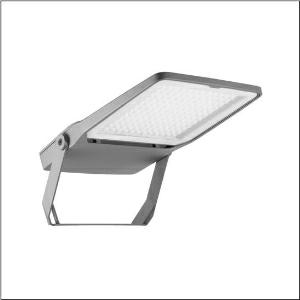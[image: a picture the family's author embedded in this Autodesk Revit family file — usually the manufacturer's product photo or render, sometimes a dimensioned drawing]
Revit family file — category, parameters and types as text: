
# Revit family: floodlight_fl_20_midi___pl43_5xa7682e2a1ac_c4a2
name_source: partatom
category: Lighting Fixtures
units: mm (PartAtom-declared; Revit-internal decimal feet)

## family parameters
Cut with Voids When Loaded = No
Host = Face
Light Source = No
Part Type = Normal
Room Calculation Point = No
Round Connector Dimension = Use Diameter
Shared = No

## types (1)
- --- (1 x LED 4000K / CRI = 70 (unbekannt), 28460 lm, 4000K)
    Apparent Load = 208 VA
    CIE Flux Codes = 32 74 99 100 100
    Color Rendering = 70
    Color Temperature = 4000K
    Default Elevation = 1800 mm
    Description = Floodlight FL 20 midi, floodlight, primary light control with lens, of plastic, primary optical cover: protective disc, of toughened safety glass, transparent, light distribution: PL43, light emission: direct distribution, primary light characteristic: asymmetric, installation type: surface-mounted, LED, High Power LED, rated luminous flux: 28.460lm, luminous efficacy: 137lm/W, light colour: 740, colour temperature: 4000K, control gear: ECG Plus, control: overheat protection, power reduction, digital communication interface, flexible luminous flux parameterisation, time-dependent luminous flux control, electronic power reduction, with terminal, 5-pole, max. 2.5mm², mains connection: 220..240V, AC, 50/60Hz, rated input power: 208W, LED unit, of diecast aluminium, powder-coated, Siteco® metallic grey (DB 702S), corrosivity category C5 mid according to DIN EN ISO 12944, incl. 1x M20 cable gland for cable Ø 6.5..12mm, length: 654mm, width: 450mm, height: 76mm, housing frame, of diecast aluminium, powder-coated, Siteco® metallic grey (DB 702S), mounting bracket, of steel, powder-coated, Siteco® metallic grey (DB 702S), DALI, protection rating (complete): IP66, insulation class (complete): insulation class II (safety insulation), certification: CE, ENEC, VDE, protection symbol: D, permissible operating ambient temperature: -40..+40°C, permissible operating ambient temperature for outdoor applications: -40..+50°C, standard: DIN EN 12944, packaging unit: 1 piece

Light Distribution: PL43
    Height = 76 mm
    Lamp = 1 x LED 4000K / CRI >= 70 (unbekannt)
    Lamp Light Flux = 28460 lm
    Lamp count = 1
    Length = 672 mm
    Luminous efficacy = 137 lm/W
    Manufacturer = Siteco
    ModVariant = No
    Model = 5XA7682E2A1AC
    Mounting Place = Wall
    Mounting Type = Surface mounted
    Number of Poles = 1
    OnlyDefault = Yes
    Power Factor = 1
    Product Name = Floodlight FL 20 midi | PL43
    Product group = floodlight | wall mounted
    ProductGroupID = 2001
    Protection Class = Protection class II
    Protection Degree = IP 66
    RLX_Detail_Level = 1
    RLX_Emergency_Light_Flux = 0 lm
    RLX_Emergency_Type = 0
    RLX_Emergency_Type_DB = No
    RlxData = <blob elided: 97693 chars, md5=61843b7a>
    Socket = socket
    Standby Power = 0 W
    System Light Flux = 28460 lm
    System Power = 208 W
    Type Comments = factory setting: luminous flux: 100 % | dim-lin: 254 | 484 mA
    Type Image = l_1005943.jpg
    URL = http://relux.com
    VarID = @adj_148329
    Voltage = 0 V
    Weight = 0.00 kg
    Width = 450 mm

## geometry (parser evidence)
native form markers: Blend x4, Sweep x12
no freeform markers — native parametric forms only
